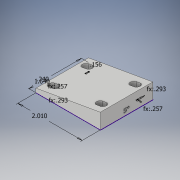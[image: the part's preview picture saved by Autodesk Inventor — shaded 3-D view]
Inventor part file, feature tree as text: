
AUTODESK INVENTOR PART (.ipt)
format: ipt  version: 2018 (Build 220112000, 112)  size: 201,728 bytes
history: native  units: in
note: dims shown in document units (in); Inventor stores cm internally (conversion verified against a paired STEP export)
features: sketch x4, extrude x3, projected_geometry x1
ambient origin geometry x8: Origin, YZ Plane, XZ Plane, XY Plane, X Axis, Y Axis, Z Axis, Center Point
bodies: Body1 (feature_tree)
feature tree (8):
  sketch  "Sketch1"  dims[d0=0.1562in d1=1.64in]
  extrude  "Extrusion8"  Depth=1.64in
  extrude  "Extrusion9"  Depth=0.24in
  extrude  "Extrusion10"  Depth=0.257in
  sketch  "Sketch10"  dims[d2=2.01in d3=0.24in]
  sketch  "Sketch11"  dims[d4=0.293in d5=0.257in]
  sketch  "Sketch13"  dims[d6=0.293in d7=0.257in d20=0.125in d21=1.25in d22=0.125in d23=0.125in d24=0.1875in d25=0.0938in d61=0.0687in d62=0.125in d63=1.64in d64=0.0in d65=0.125in d66=0.0995in d67=1.64in d68=0.0in d69=0.08in d70=0.015in d71=0.0in]
  projected_geometry  "Projected Loop1"
